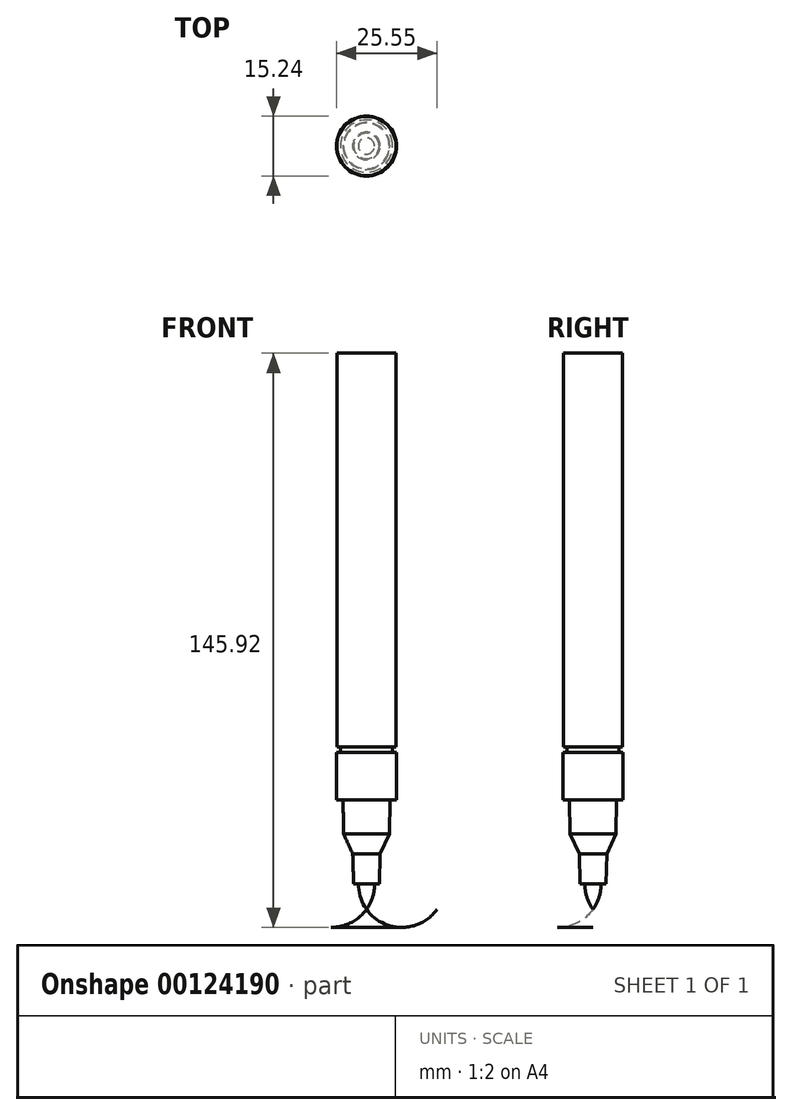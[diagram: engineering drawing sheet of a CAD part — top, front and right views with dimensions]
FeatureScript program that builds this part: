
annotation { "Feature Type Name" : "Feature", "Feature Type Description" : "" }
export const myFeature = defineFeature(function(context is Context, id is Id, definition is map)
    precondition{}
    {
        {
            var Q0;
            Q0=qCreatedBy(makeId("Top.planeOp"),FACE);
            var sketch = newSketch(context, id + "F0", { "sketchPlane" : qUnion([Q0])});
            skCircle(sketch, "E0", {"center": v(0, 0) * mm, "radius": 7.5 * mm});
            skSolve(sketch);
        }
        {
            var Q0;
            Q0 = qSketchRegion(id + "F0", true);
            extrude(context, id + "F1", {"entities" : qUnion([Q0]), "depth" : 100 * mm});
        }
        {
            var Q0;
            Q0=makeQuery(id+"F1.opExtrude","CAP_FACE",FACE,{"disambiguationData":[OSD([sQuery(id+"F0.wireOp",EDGE,"E0")])],"isStart":true});
            var sketch = newSketch(context, id + "F2", { "sketchPlane" : qUnion([Q0])});
            skCircle(sketch, "E1", {"center": v(0, 0) * mm, "radius": 6.65 * mm});
            skSolve(sketch);
        }
        {
            var Q0;
            Q0 = qSketchRegion(id + "F2", true);
            extrude(context, id + "F3", {"entities" : qUnion([Q0]), "operationType" : NewBodyOperationType.ADD, "depth" : 1.5 * mm});
        }
        {
            var Q0;
            Q0=makeQuery(id+"F3.opExtrude","CAP_FACE",FACE,{"disambiguationData":[OSD([sQuery(id+"F2.wireOp",EDGE,"E1")])],"isStart":false});
            var sketch = newSketch(context, id + "F4", { "sketchPlane" : qUnion([Q0])});
            skCircle(sketch, "E2", {"center": v(0, 0) * mm, "radius": 7.62 * mm});
            skSolve(sketch);
        }
        {
            var Q0;
            Q0 = qSketchRegion(id + "F4", true);
            extrude(context, id + "F5", {"entities" : qUnion([Q0]), "operationType" : NewBodyOperationType.ADD, "depth" : 12 * mm});
        }
        {
            var Q0;
            Q0=makeQuery(id+"F5.opExtrude","CAP_FACE",FACE,{"disambiguationData":[OSD([sQuery(id+"F4.wireOp",EDGE,"E2")])],"isStart":false});
            var sketch = newSketch(context, id + "F6", { "sketchPlane" : qUnion([Q0])});
            skCircle(sketch, "E3", {"center": v(0, 0) * mm, "radius": 5.95 * mm});
            skSolve(sketch);
        }
        {
            var Q0;
            Q0=makeQuery(id+"F6.imprint","IMPRINT",FACE,{"disambiguationData":[TD([[makeQuery(id+"F6.imprint","IMPRINT",EDGE,{"derivedFrom":sQuery(id+"F6.wireOp",EDGE,"E3")}),1.0]])]});
            cPlane(context, id + "F7", {"entities" : qUnion([Q0]), "cplaneType" : CPlaneType.OFFSET, "offset" : 8.7 * mm, "width" : 150 * mm, "height" : 150 * mm});
        }
        {
            var Q0;
            Q0=qCreatedBy(id+"F7.planeOp",FACE);
            var sketch = newSketch(context, id + "F8", { "sketchPlane" : qUnion([Q0])});
            skCircle(sketch, "E4", {"center": v(0, 0) * mm, "radius": 5.8 * mm});
            skSolve(sketch);
        }
        {
            var Q1;
            Q1=makeQuery(id+"F6.imprint","IMPRINT",FACE,{"disambiguationData":[TD([[makeQuery(id+"F6.imprint","IMPRINT",EDGE,{"derivedFrom":sQuery(id+"F6.wireOp",EDGE,"E3")}),1.0]])]});
            var Q2;
            Q2=makeQuery(id+"F8.imprint","IMPRINT",FACE,{"disambiguationData":[TD([[makeQuery(id+"F8.imprint","IMPRINT",EDGE,{"derivedFrom":sQuery(id+"F8.wireOp",EDGE,"E4")}),1.0]])]});
            loft(context, id + "F9", {"operationType" : NewBodyOperationType.ADD, "sheetProfilesArray" : [{ "sheetProfileEntities" : qUnion([Q1]) }, { "sheetProfileEntities" : qUnion([Q2]) }]});
        }
        {
            var Q0;
            Q0=qCreatedBy(id+"F7.planeOp",FACE);
            cPlane(context, id + "F10", {"entities" : qUnion([Q0]), "cplaneType" : CPlaneType.OFFSET, "offset" : 5 * mm, "width" : 150 * mm, "height" : 150 * mm});
        }
        {
            var Q0;
            Q0=qCreatedBy(id+"F10.planeOp",FACE);
            var sketch = newSketch(context, id + "F11", { "sketchPlane" : qUnion([Q0])});
            skCircle(sketch, "E5", {"center": v(0, 0) * mm, "radius": 3.5 * mm});
            skSolve(sketch);
        }
        {
            var Q1;
            Q1=makeQuery(id+"F9.opLoft","CAP_FACE",FACE,{"disambiguationData":[OSD([makeQuery(id+"F8.imprint","IMPRINT",FACE,{"disambiguationData":[TD([[makeQuery(id+"F8.imprint","IMPRINT",EDGE,{"derivedFrom":sQuery(id+"F8.wireOp",EDGE,"E4")}),1.0]])]})])],"isStart":true});
            var Q2;
            Q2=makeQuery(id+"F11.imprint","IMPRINT",FACE,{"disambiguationData":[TD([[makeQuery(id+"F11.imprint","IMPRINT",EDGE,{"derivedFrom":sQuery(id+"F11.wireOp",EDGE,"E5")}),1.0]])]});
            loft(context, id + "F12", {"operationType" : NewBodyOperationType.ADD, "sheetProfilesArray" : [{ "sheetProfileEntities" : qUnion([Q1]) }, { "sheetProfileEntities" : qUnion([Q2]) }]});
        }
        {
            var Q0;
            Q0=qCreatedBy(id+"F10.planeOp",FACE);
            cPlane(context, id + "F13", {"entities" : qUnion([Q0]), "cplaneType" : CPlaneType.OFFSET, "offset" : 7.7 * mm, "width" : 150 * mm, "height" : 150 * mm});
        }
        {
            var Q0;
            Q0=qCreatedBy(id+"F13.planeOp",FACE);
            var sketch = newSketch(context, id + "F14", { "sketchPlane" : qUnion([Q0])});
            skCircle(sketch, "E6", {"center": v(0, 0) * mm, "radius": 3.25 * mm});
            skSolve(sketch);
        }
        {
            var Q1;
            Q1=makeQuery(id+"F12.opLoft","CAP_FACE",FACE,{"disambiguationData":[OSD([makeQuery(id+"F11.imprint","IMPRINT",FACE,{"disambiguationData":[TD([[makeQuery(id+"F11.imprint","IMPRINT",EDGE,{"derivedFrom":sQuery(id+"F11.wireOp",EDGE,"E5")}),1.0]])]})])],"isStart":true});
            var Q2;
            Q2=makeQuery(id+"F14.imprint","IMPRINT",FACE,{"disambiguationData":[TD([[makeQuery(id+"F14.imprint","IMPRINT",EDGE,{"derivedFrom":sQuery(id+"F14.wireOp",EDGE,"E6")}),1.0]])]});
            loft(context, id + "F15", {"operationType" : NewBodyOperationType.ADD, "sheetProfilesArray" : [{ "sheetProfileEntities" : qUnion([Q1]) }, { "sheetProfileEntities" : qUnion([Q2]) }]});
        }
        {
            var Q0;
            Q0=qCreatedBy(makeId("Right.planeOp"),FACE);
            var sketch = newSketch(context, id + "F16", { "sketchPlane" : qUnion([Q0])});
            skArc(sketch, "E7", {"start": v(-2.05, -34.9) * mm, "mid": v(-1.52, -38.26) * mm, "end": v(0, -41.3) * mm});
            skLineSegment(sketch, "E8", {"start": v(0, -34.9) * mm, "end": v(0, -41.3) * mm});
            skLineSegment(sketch, "E9", {"start": v(-2.05, -34.9) * mm, "end": v(-2.05, -37.03) * mm, "construction": true});
            skLineSegment(sketch, "E10", {"start": v(-2.05, -34.9) * mm, "end": v(0, -34.9) * mm});
            skSolve(sketch);
        }
        {
            var Q0;
            Q0=makeQuery(id+"F16.imprint","IMPRINT",FACE,{"disambiguationData":[TD([[makeQuery(id+"F16.imprint","IMPRINT",EDGE,{"derivedFrom":sQuery(id+"F16.wireOp",EDGE,"E7")}),1.0]])]});
            var Q1;
            Q1=sQuery(id+"F16.wireOp",EDGE,"E8");
            revolve(context, id + "F17", {"operationType" : NewBodyOperationType.ADD, "entities" : qUnion([Q0]), "axis" : qUnion([Q1]), "revolveType" : RevolveType.FULL});
        }
    });
